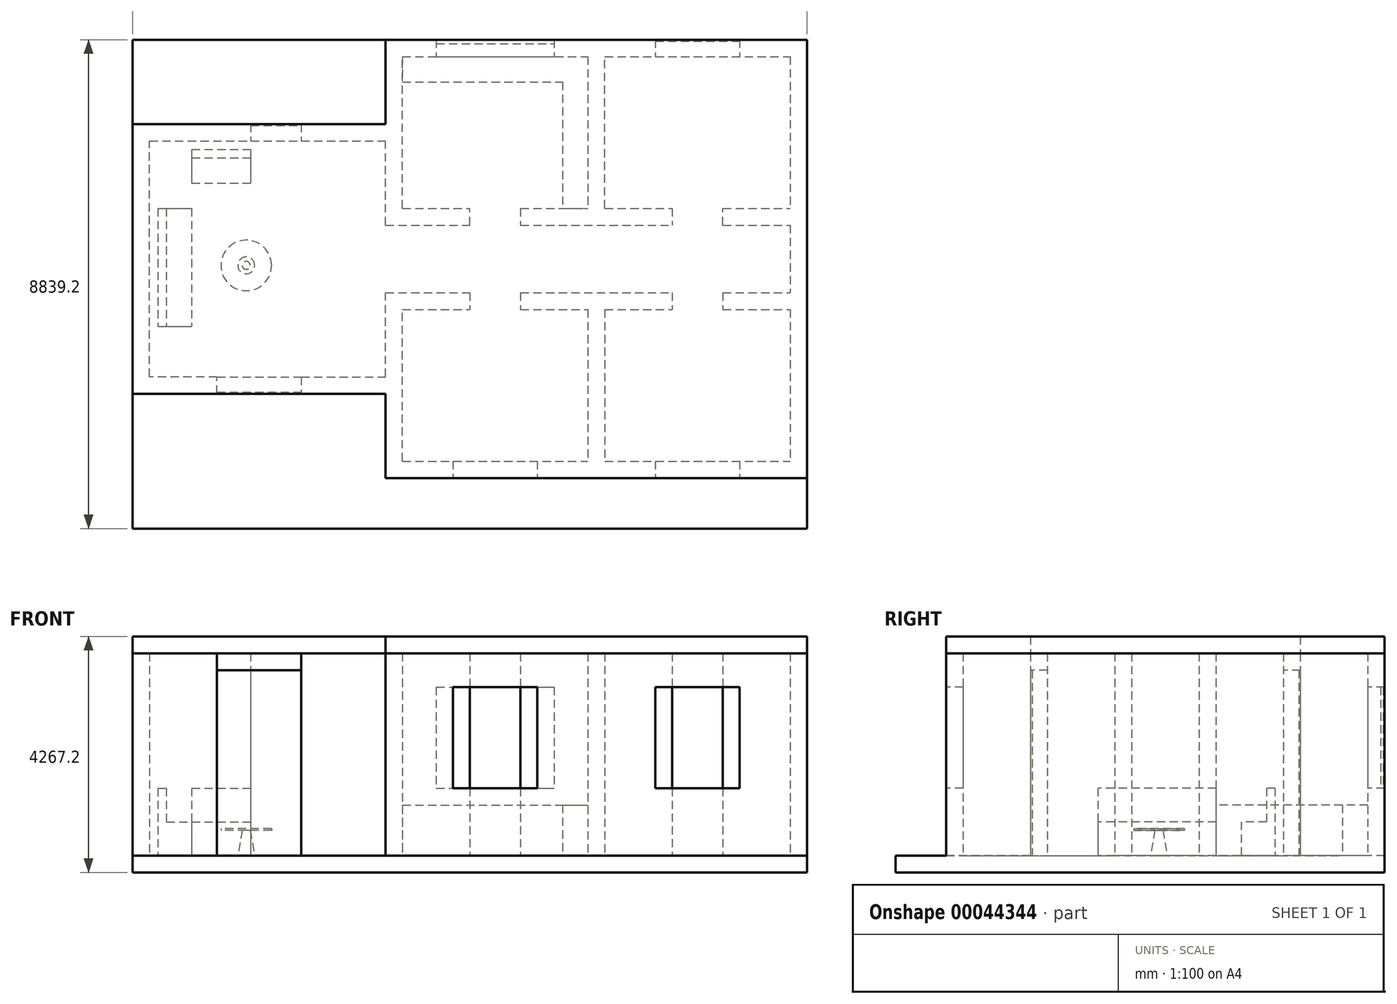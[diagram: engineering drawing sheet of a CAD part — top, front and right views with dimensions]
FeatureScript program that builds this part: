
annotation { "Feature Type Name" : "Feature", "Feature Type Description" : "" }
export const myFeature = defineFeature(function(context is Context, id is Id, definition is map)
    precondition{}
    {
        {
            var Q0;
            Q0=qCreatedBy(makeId("Top.planeOp"),FACE);
            var sketch = newSketch(context, id + "F0", { "sketchPlane" : qUnion([Q0])});
            skLineSegment(sketch, "E0", {"start": v(-1524, -1642.32) * mm, "end": v(0, -1642.32) * mm});
            skLineSegment(sketch, "E1", {"start": v(0, -1642.32) * mm, "end": v(0, -1337.52) * mm});
            skLineSegment(sketch, "E2", {"start": v(0, -1337.52) * mm, "end": v(-1524, -1337.52) * mm});
            skLineSegment(sketch, "E3", {"start": v(-1524, -1337.52) * mm, "end": v(-1524, -1642.32) * mm});
            skLineSegment(sketch, "E4.bottom", {"start": v(1524, -1337.52) * mm, "end": v(3048, -1337.52) * mm});
            skLineSegment(sketch, "E4.top", {"start": v(1524, -1642.32) * mm, "end": v(3048, -1642.32) * mm});
            skLineSegment(sketch, "E4.left", {"start": v(1524, -1337.52) * mm, "end": v(1524, -1642.32) * mm});
            skLineSegment(sketch, "E4.right", {"start": v(3048, -1337.52) * mm, "end": v(3048, -1642.32) * mm});
            skLineSegment(sketch, "E5.bottom", {"start": v(-1524, -1337.52) * mm, "end": v(-1219.2, -1337.52) * mm});
            skLineSegment(sketch, "E5.top", {"start": v(-1524, 3234.48) * mm, "end": v(-1219.2, 3234.48) * mm});
            skLineSegment(sketch, "E5.left", {"start": v(-1524, -1337.52) * mm, "end": v(-1524, 3234.48) * mm});
            skLineSegment(sketch, "E5.right", {"start": v(-1219.2, -1337.52) * mm, "end": v(-1219.2, 3234.48) * mm});
            skLineSegment(sketch, "E6.bottom", {"start": v(-1219.2, 3234.48) * mm, "end": v(609.6, 3234.48) * mm});
            skLineSegment(sketch, "E6.top", {"start": v(-1219.2, 2929.68) * mm, "end": v(609.6, 2929.68) * mm});
            skLineSegment(sketch, "E6.left", {"start": v(-1219.2, 3234.48) * mm, "end": v(-1219.2, 2929.68) * mm});
            skLineSegment(sketch, "E6.right", {"start": v(609.6, 3234.48) * mm, "end": v(609.6, 2929.68) * mm});
            skLineSegment(sketch, "E7.bottom", {"start": v(1524, 3234.48) * mm, "end": v(3048, 3234.48) * mm});
            skLineSegment(sketch, "E7.top", {"start": v(1524, 2929.68) * mm, "end": v(3048, 2929.68) * mm});
            skLineSegment(sketch, "E7.left", {"start": v(1524, 3234.48) * mm, "end": v(1524, 2929.68) * mm});
            skLineSegment(sketch, "E7.right", {"start": v(3048, 3234.48) * mm, "end": v(3048, 2929.68) * mm});
            skLineSegment(sketch, "E8.bottom", {"start": v(3048, -3166.32) * mm, "end": v(3352.8, -3166.32) * mm});
            skLineSegment(sketch, "E8.top", {"start": v(3048, 186.48) * mm, "end": v(3352.8, 186.48) * mm});
            skLineSegment(sketch, "E8.left", {"start": v(3048, -3166.32) * mm, "end": v(3048, 186.48) * mm});
            skLineSegment(sketch, "E8.right", {"start": v(3352.8, -3166.32) * mm, "end": v(3352.8, 186.48) * mm});
            skLineSegment(sketch, "E9.bottom", {"start": v(3352.8, 1405.68) * mm, "end": v(3048, 1405.68) * mm});
            skLineSegment(sketch, "E9.top", {"start": v(3352.8, 4758.48) * mm, "end": v(3048, 4758.48) * mm});
            skLineSegment(sketch, "E9.left", {"start": v(3352.8, 1405.68) * mm, "end": v(3352.8, 4758.48) * mm});
            skLineSegment(sketch, "E9.right", {"start": v(3048, 1405.68) * mm, "end": v(3048, 4758.48) * mm});
            skLineSegment(sketch, "E10.bottom", {"start": v(3352.8, 1405.68) * mm, "end": v(4572, 1405.68) * mm});
            skLineSegment(sketch, "E10.top", {"start": v(3352.8, 1710.48) * mm, "end": v(4572, 1710.48) * mm});
            skLineSegment(sketch, "E10.left", {"start": v(3352.8, 1405.68) * mm, "end": v(3352.8, 1710.48) * mm});
            skLineSegment(sketch, "E10.right", {"start": v(4572, 1405.68) * mm, "end": v(4572, 1710.48) * mm});
            skLineSegment(sketch, "E11.bottom", {"start": v(5486.4, 1710.48) * mm, "end": v(6705.6, 1710.48) * mm});
            skLineSegment(sketch, "E11.top", {"start": v(5486.4, 1405.68) * mm, "end": v(6705.6, 1405.68) * mm});
            skLineSegment(sketch, "E11.left", {"start": v(5486.4, 1710.48) * mm, "end": v(5486.4, 1405.68) * mm});
            skLineSegment(sketch, "E11.right", {"start": v(6705.6, 1710.48) * mm, "end": v(6705.6, 1405.68) * mm});
            skLineSegment(sketch, "E12.bottom", {"start": v(6705.6, 1405.68) * mm, "end": v(7010.4, 1405.68) * mm});
            skLineSegment(sketch, "E12.top", {"start": v(6705.6, 4758.48) * mm, "end": v(7010.4, 4758.48) * mm});
            skLineSegment(sketch, "E12.left", {"start": v(6705.6, 1405.68) * mm, "end": v(6705.6, 4758.48) * mm});
            skLineSegment(sketch, "E12.right", {"start": v(7010.4, 1405.68) * mm, "end": v(7010.4, 4758.48) * mm});
            skLineSegment(sketch, "E13.bottom", {"start": v(3352.8, 4758.48) * mm, "end": v(3962.4, 4758.48) * mm});
            skLineSegment(sketch, "E13.top", {"start": v(3352.8, 4453.68) * mm, "end": v(3962.4, 4453.68) * mm});
            skLineSegment(sketch, "E13.left", {"start": v(3352.8, 4758.48) * mm, "end": v(3352.8, 4453.68) * mm});
            skLineSegment(sketch, "E13.right", {"start": v(3962.4, 4758.48) * mm, "end": v(3962.4, 4453.68) * mm});
            skLineSegment(sketch, "E14.bottom", {"start": v(6096, 4758.48) * mm, "end": v(6705.6, 4758.48) * mm});
            skLineSegment(sketch, "E14.top", {"start": v(6096, 4453.68) * mm, "end": v(6705.6, 4453.68) * mm});
            skLineSegment(sketch, "E14.left", {"start": v(6096, 4758.48) * mm, "end": v(6096, 4453.68) * mm});
            skLineSegment(sketch, "E14.right", {"start": v(6705.6, 4758.48) * mm, "end": v(6705.6, 4453.68) * mm});
            skLineSegment(sketch, "E15.bottom", {"start": v(3352.8, 186.48) * mm, "end": v(4572, 186.48) * mm});
            skLineSegment(sketch, "E15.top", {"start": v(3352.8, -118.32) * mm, "end": v(4572, -118.32) * mm});
            skLineSegment(sketch, "E15.left", {"start": v(3352.8, 186.48) * mm, "end": v(3352.8, -118.32) * mm});
            skLineSegment(sketch, "E15.right", {"start": v(4572, 186.48) * mm, "end": v(4572, -118.32) * mm});
            skLineSegment(sketch, "E16.bottom", {"start": v(5486.4, 186.48) * mm, "end": v(6705.6, 186.48) * mm});
            skLineSegment(sketch, "E16.top", {"start": v(5486.4, -118.32) * mm, "end": v(6705.6, -118.32) * mm});
            skLineSegment(sketch, "E16.left", {"start": v(5486.4, 186.48) * mm, "end": v(5486.4, -118.32) * mm});
            skLineSegment(sketch, "E16.right", {"start": v(6705.6, 186.48) * mm, "end": v(6705.6, -118.32) * mm});
            skLineSegment(sketch, "E17.bottom", {"start": v(6705.6, 186.48) * mm, "end": v(7010.4, 186.48) * mm});
            skLineSegment(sketch, "E17.top", {"start": v(6705.6, -3166.32) * mm, "end": v(7010.4, -3166.32) * mm});
            skLineSegment(sketch, "E17.left", {"start": v(6705.6, 186.48) * mm, "end": v(6705.6, -3166.32) * mm});
            skLineSegment(sketch, "E17.right", {"start": v(7010.4, 186.48) * mm, "end": v(7010.4, -3166.32) * mm});
            skLineSegment(sketch, "E18.left", {"start": v(3352.8, -3166.32) * mm, "end": v(3352.8, -2861.52) * mm});
            skLineSegment(sketch, "E19.left", {"start": v(6705.6, -3166.32) * mm, "end": v(6705.6, -2861.52) * mm});
            skLineSegment(sketch, "E20.bottom", {"start": v(7010.4, 4758.48) * mm, "end": v(7924.8, 4758.48) * mm});
            skLineSegment(sketch, "E20.top", {"start": v(7010.4, 4453.68) * mm, "end": v(7924.8, 4453.68) * mm});
            skLineSegment(sketch, "E20.left", {"start": v(7010.4, 4758.48) * mm, "end": v(7010.4, 4453.68) * mm});
            skLineSegment(sketch, "E20.right", {"start": v(7924.8, 4758.48) * mm, "end": v(7924.8, 4453.68) * mm});
            skLineSegment(sketch, "E21.bottom", {"start": v(9448.8, 4758.48) * mm, "end": v(10363.2, 4758.48) * mm});
            skLineSegment(sketch, "E21.top", {"start": v(9448.8, 4453.68) * mm, "end": v(10363.2, 4453.68) * mm});
            skLineSegment(sketch, "E21.left", {"start": v(9448.8, 4758.48) * mm, "end": v(9448.8, 4453.68) * mm});
            skLineSegment(sketch, "E21.right", {"start": v(10363.2, 4758.48) * mm, "end": v(10363.2, 4453.68) * mm});
            skLineSegment(sketch, "E22.bottom", {"start": v(10363.2, 4758.48) * mm, "end": v(10668, 4758.48) * mm});
            skLineSegment(sketch, "E22.top", {"start": v(10363.2, 1405.68) * mm, "end": v(10668, 1405.68) * mm});
            skLineSegment(sketch, "E22.left", {"start": v(10363.2, 4758.48) * mm, "end": v(10363.2, 1405.68) * mm});
            skLineSegment(sketch, "E22.right", {"start": v(10668, 4758.48) * mm, "end": v(10668, 1405.68) * mm});
            skPoint(sketch, "E23.oppositeSnap0", {"position": v(6858, 1405.68) * mm});
            skLineSegment(sketch, "E23.bottom", {"start": v(7010.4, 1710.48) * mm, "end": v(8229.6, 1710.48) * mm});
            skLineSegment(sketch, "E23.top", {"start": v(7010.4, 1405.68) * mm, "end": v(8229.6, 1405.68) * mm});
            skLineSegment(sketch, "E23.left", {"start": v(7010.4, 1710.48) * mm, "end": v(7010.4, 1405.68) * mm});
            skLineSegment(sketch, "E23.right", {"start": v(8229.6, 1710.48) * mm, "end": v(8229.6, 1405.68) * mm});
            skLineSegment(sketch, "E24.bottom", {"start": v(9144, 1405.68) * mm, "end": v(10363.2, 1405.68) * mm});
            skLineSegment(sketch, "E24.top", {"start": v(9144, 1710.48) * mm, "end": v(10363.2, 1710.48) * mm});
            skLineSegment(sketch, "E24.left", {"start": v(9144, 1405.68) * mm, "end": v(9144, 1710.48) * mm});
            skLineSegment(sketch, "E24.right", {"start": v(10363.2, 1405.68) * mm, "end": v(10363.2, 1710.48) * mm});
            skLineSegment(sketch, "E25.bottom", {"start": v(7010.4, 186.48) * mm, "end": v(8229.6, 186.48) * mm});
            skLineSegment(sketch, "E25.top", {"start": v(7010.4, -118.32) * mm, "end": v(8229.6, -118.32) * mm});
            skLineSegment(sketch, "E25.left", {"start": v(7010.4, 186.48) * mm, "end": v(7010.4, -118.32) * mm});
            skLineSegment(sketch, "E25.right", {"start": v(8229.6, 186.48) * mm, "end": v(8229.6, -118.32) * mm});
            skLineSegment(sketch, "E26.bottom", {"start": v(9144, 186.48) * mm, "end": v(10363.2, 186.48) * mm});
            skLineSegment(sketch, "E26.top", {"start": v(9144, -118.32) * mm, "end": v(10363.2, -118.32) * mm});
            skLineSegment(sketch, "E26.left", {"start": v(9144, 186.48) * mm, "end": v(9144, -118.32) * mm});
            skLineSegment(sketch, "E26.right", {"start": v(10363.2, 186.48) * mm, "end": v(10363.2, -118.32) * mm});
            skLineSegment(sketch, "E27.bottom", {"start": v(7010.4, -3166.32) * mm, "end": v(7924.8, -3166.32) * mm});
            skLineSegment(sketch, "E27.top", {"start": v(7010.4, -2861.52) * mm, "end": v(7924.8, -2861.52) * mm});
            skLineSegment(sketch, "E27.left", {"start": v(7010.4, -3166.32) * mm, "end": v(7010.4, -2861.52) * mm});
            skLineSegment(sketch, "E27.right", {"start": v(7924.8, -3166.32) * mm, "end": v(7924.8, -2861.52) * mm});
            skLineSegment(sketch, "E28.bottom", {"start": v(9448.8, -2861.52) * mm, "end": v(10363.2, -2861.52) * mm});
            skLineSegment(sketch, "E28.top", {"start": v(9448.8, -3166.32) * mm, "end": v(10363.2, -3166.32) * mm});
            skLineSegment(sketch, "E28.left", {"start": v(9448.8, -2861.52) * mm, "end": v(9448.8, -3166.32) * mm});
            skLineSegment(sketch, "E28.right", {"start": v(10363.2, -2861.52) * mm, "end": v(10363.2, -3166.32) * mm});
            skLineSegment(sketch, "E29.top", {"start": v(10363.2, -3166.32) * mm, "end": v(10668, -3166.32) * mm});
            skLineSegment(sketch, "E29.left", {"start": v(10363.2, 1405.68) * mm, "end": v(10363.2, -3166.32) * mm});
            skLineSegment(sketch, "E29.right", {"start": v(10668, 1405.68) * mm, "end": v(10668, -3166.32) * mm});
            skLineSegment(sketch, "E30.bottom", {"start": v(3352.8, -2861.52) * mm, "end": v(4267.2, -2861.52) * mm});
            skLineSegment(sketch, "E30.top", {"start": v(3352.8, -3166.32) * mm, "end": v(4267.2, -3166.32) * mm});
            skLineSegment(sketch, "E30.left", {"start": v(3352.8, -2861.52) * mm, "end": v(3352.8, -3166.32) * mm});
            skLineSegment(sketch, "E30.right", {"start": v(4267.2, -2861.52) * mm, "end": v(4267.2, -3166.32) * mm});
            skLineSegment(sketch, "E31.bottom", {"start": v(6705.6, -2861.52) * mm, "end": v(5791.2, -2861.52) * mm});
            skLineSegment(sketch, "E31.top", {"start": v(6705.6, -3166.32) * mm, "end": v(5791.2, -3166.32) * mm});
            skLineSegment(sketch, "E31.left", {"start": v(6705.6, -2861.52) * mm, "end": v(6705.6, -3166.32) * mm});
            skLineSegment(sketch, "E31.right", {"start": v(5791.2, -2861.52) * mm, "end": v(5791.2, -3166.32) * mm});
            skSolve(sketch);
        }
        {
            var Q0;
            Q0 = qSketchRegion(id + "F0", true);
            extrude(context, id + "F1", {"entities" : qUnion([Q0]), "depth" : 3657.6 * mm});
        }
        {
            var Q0;
            Q0=qCreatedBy(makeId("Top.planeOp"),FACE);
            var sketch = newSketch(context, id + "F2", { "sketchPlane" : qUnion([Q0])});
            skLineSegment(sketch, "E32.bottom", {"start": v(-1524, 4758.48) * mm, "end": v(10668, 4758.48) * mm});
            skLineSegment(sketch, "E32.top", {"start": v(-1524, -3166.32) * mm, "end": v(10668, -3166.32) * mm});
            skLineSegment(sketch, "E32.left", {"start": v(-1524, 4758.48) * mm, "end": v(-1524, -3166.32) * mm});
            skLineSegment(sketch, "E32.right", {"start": v(10668, 4758.48) * mm, "end": v(10668, -3166.32) * mm});
            skLineSegment(sketch, "E33.top", {"start": v(-1524, -4080.72) * mm, "end": v(10668, -4080.72) * mm});
            skLineSegment(sketch, "E33.left", {"start": v(-1524, -3166.32) * mm, "end": v(-1524, -4080.72) * mm});
            skLineSegment(sketch, "E33.right", {"start": v(10668, -3166.32) * mm, "end": v(10668, -4080.72) * mm});
            skSolve(sketch);
        }
        {
            var Q0;
            Q0 = qSketchRegion(id + "F2", true);
            extrude(context, id + "F3", {"entities" : qUnion([Q0]), "oppositeDirection" : true, "depth" : 304.8 * mm});
        }
        {
            var Q0;
            Q0=qCreatedBy(makeId("Top.planeOp"),FACE);
            var sketch = newSketch(context, id + "F4", { "sketchPlane" : qUnion([Q0])});
            skLineSegment(sketch, "E34.bottom", {"start": v(3962.4, 4758.48) * mm, "end": v(6096, 4758.48) * mm});
            skLineSegment(sketch, "E34.top", {"start": v(3962.4, 4453.68) * mm, "end": v(6096, 4453.68) * mm});
            skLineSegment(sketch, "E34.left", {"start": v(3962.4, 4758.48) * mm, "end": v(3962.4, 4453.68) * mm});
            skLineSegment(sketch, "E34.right", {"start": v(6096, 4758.48) * mm, "end": v(6096, 4453.68) * mm});
            skLineSegment(sketch, "E35.bottom", {"start": v(7924.8, -2861.52) * mm, "end": v(9448.8, -2861.52) * mm});
            skLineSegment(sketch, "E35.top", {"start": v(7924.8, -3166.32) * mm, "end": v(9448.8, -3166.32) * mm});
            skLineSegment(sketch, "E35.left", {"start": v(7924.8, -2861.52) * mm, "end": v(7924.8, -3166.32) * mm});
            skLineSegment(sketch, "E35.right", {"start": v(9448.8, -2861.52) * mm, "end": v(9448.8, -3166.32) * mm});
            skLineSegment(sketch, "E36.bottom", {"start": v(4267.2, -2861.52) * mm, "end": v(5791.2, -2861.52) * mm});
            skLineSegment(sketch, "E36.top", {"start": v(4267.2, -3166.32) * mm, "end": v(5791.2, -3166.32) * mm});
            skLineSegment(sketch, "E36.left", {"start": v(4267.2, -2861.52) * mm, "end": v(4267.2, -3166.32) * mm});
            skLineSegment(sketch, "E36.right", {"start": v(5791.2, -2861.52) * mm, "end": v(5791.2, -3166.32) * mm});
            skSolve(sketch);
        }
        {
            var Q0;
            Q0 = qSketchRegion(id + "F4", true);
            extrude(context, id + "F5", {"entities" : qUnion([Q0]), "depth" : 1219.2 * mm});
        }
        {
            var Q0;
            Q0=qCreatedBy(makeId("Top.planeOp"),FACE);
            cPlane(context, id + "F6", {"entities" : qUnion([Q0]), "cplaneType" : CPlaneType.OFFSET, "offset" : 3048 * mm, "width" : 152.4 * mm, "height" : 152.4 * mm});
        }
        {
            var Q0;
            Q0=qCreatedBy(id+"F6.planeOp",FACE);
            var sketch = newSketch(context, id + "F7", { "sketchPlane" : qUnion([Q0])});
            skLineSegment(sketch, "E37.bottom", {"start": v(3962.4, 4758.48) * mm, "end": v(6096, 4758.48) * mm});
            skLineSegment(sketch, "E37.top", {"start": v(3962.4, 4453.68) * mm, "end": v(6096, 4453.68) * mm});
            skLineSegment(sketch, "E37.left", {"start": v(3962.4, 4758.48) * mm, "end": v(3962.4, 4453.68) * mm});
            skLineSegment(sketch, "E37.right", {"start": v(6096, 4758.48) * mm, "end": v(6096, 4453.68) * mm});
            skLineSegment(sketch, "E38.bottom", {"start": v(7924.8, 4758.48) * mm, "end": v(9448.8, 4758.48) * mm});
            skLineSegment(sketch, "E38.top", {"start": v(7924.8, 4453.68) * mm, "end": v(9448.8, 4453.68) * mm});
            skLineSegment(sketch, "E38.left", {"start": v(7924.8, 4758.48) * mm, "end": v(7924.8, 4453.68) * mm});
            skLineSegment(sketch, "E38.right", {"start": v(9448.8, 4758.48) * mm, "end": v(9448.8, 4453.68) * mm});
            skLineSegment(sketch, "E39.bottom", {"start": v(7924.8, -2861.52) * mm, "end": v(9448.8, -2861.52) * mm});
            skLineSegment(sketch, "E39.top", {"start": v(7924.8, -3166.32) * mm, "end": v(9448.8, -3166.32) * mm});
            skLineSegment(sketch, "E39.left", {"start": v(7924.8, -2861.52) * mm, "end": v(7924.8, -3166.32) * mm});
            skLineSegment(sketch, "E39.right", {"start": v(9448.8, -2861.52) * mm, "end": v(9448.8, -3166.32) * mm});
            skLineSegment(sketch, "E40.bottom", {"start": v(4267.2, -2861.52) * mm, "end": v(5791.2, -2861.52) * mm});
            skLineSegment(sketch, "E40.top", {"start": v(4267.2, -3166.32) * mm, "end": v(5791.2, -3166.32) * mm});
            skLineSegment(sketch, "E40.left", {"start": v(4267.2, -2861.52) * mm, "end": v(4267.2, -3166.32) * mm});
            skLineSegment(sketch, "E40.right", {"start": v(5791.2, -2861.52) * mm, "end": v(5791.2, -3166.32) * mm});
            skSolve(sketch);
        }
        {
            var Q0;
            Q0 = qSketchRegion(id + "F7", true);
            var Q1;
            Q1=makeQuery(id+"F1.opExtrude","CAP_FACE",FACE,{"disambiguationData":[OSD([sQuery(id+"F0.wireOp",EDGE,"E4.bottom"),sQuery(id+"F0.wireOp",EDGE,"E4.top"),sQuery(id+"F0.wireOp",EDGE,"E4.left"),sQuery(id+"F0.wireOp",EDGE,"E8.bottom"),sQuery(id+"F0.wireOp",EDGE,"E8.top"),sQuery(id+"F0.wireOp",EDGE,"E8.left"),sQuery(id+"F0.wireOp",EDGE,"E8.right"),sQuery(id+"F0.wireOp",EDGE,"E15.bottom"),sQuery(id+"F0.wireOp",EDGE,"E15.top"),sQuery(id+"F0.wireOp",EDGE,"E15.right"),sQuery(id+"F0.wireOp",EDGE,"E18.bottom"),sQuery(id+"F0.wireOp",EDGE,"E18.top"),sQuery(id+"F0.wireOp",EDGE,"E18.right")])],"isStart":false});
            extrude(context, id + "F8", {"entities" : qUnion([Q0]), "depth" : 609.6 * mm});
        }
        {
            var Q0;
            Q0=qCreatedBy(makeId("Top.planeOp"),FACE);
            cPlane(context, id + "F9", {"entities" : qUnion([Q0]), "cplaneType" : CPlaneType.OFFSET, "offset" : 3657.6 * mm, "width" : 152.4 * mm, "height" : 152.4 * mm});
        }
        {
            var Q0;
            Q0=qCreatedBy(id+"F9.planeOp",FACE);
            var sketch = newSketch(context, id + "F10", { "sketchPlane" : qUnion([Q0])});
            skLineSegment(sketch, "E41", {"start": v(-1524, 3234.48) * mm, "end": v(-1524, -1642.32) * mm});
            skLineSegment(sketch, "E42", {"start": v(-1524, -1642.32) * mm, "end": v(3048, -1642.32) * mm});
            skLineSegment(sketch, "E43", {"start": v(3048, -1642.32) * mm, "end": v(3048, -3166.32) * mm});
            skLineSegment(sketch, "E44", {"start": v(3048, -3166.32) * mm, "end": v(10668, -3166.32) * mm});
            skLineSegment(sketch, "E45", {"start": v(10668, -3166.32) * mm, "end": v(10668, 4758.48) * mm});
            skLineSegment(sketch, "E46", {"start": v(10668, 4758.48) * mm, "end": v(3048, 4758.48) * mm});
            skLineSegment(sketch, "E47", {"start": v(3048, 4758.48) * mm, "end": v(3048, 3234.48) * mm});
            skLineSegment(sketch, "E48", {"start": v(3048, 3234.48) * mm, "end": v(-1524, 3234.48) * mm});
            skSolve(sketch);
        }
        {
            var Q0;
            Q0 = qSketchRegion(id + "F10", true);
            extrude(context, id + "F11", {"entities" : qUnion([Q0]), "depth" : 304.8 * mm});
        }
        {
            var Q0;
            Q0=makeQuery(id+"F1.opExtrude","SWEPT_BODY",BODY,{"disambiguationData":[OSD([sQuery(id+"F0.wireOp",EDGE,"E0"),sQuery(id+"F0.wireOp",EDGE,"E1"),sQuery(id+"F0.wireOp",EDGE,"E2"),sQuery(id+"F0.wireOp",EDGE,"E3"),sQuery(id+"F0.wireOp",EDGE,"E5.top"),sQuery(id+"F0.wireOp",EDGE,"E5.left"),sQuery(id+"F0.wireOp",EDGE,"E5.right"),sQuery(id+"F0.wireOp",EDGE,"E6.bottom"),sQuery(id+"F0.wireOp",EDGE,"E6.top"),sQuery(id+"F0.wireOp",EDGE,"E6.right")])]});
            var Q1;
            Q1=makeQuery(id+"F1.opExtrude","SWEPT_BODY",BODY,{"disambiguationData":[OSD([sQuery(id+"F0.wireOp",EDGE,"E4.bottom"),sQuery(id+"F0.wireOp",EDGE,"E4.top"),sQuery(id+"F0.wireOp",EDGE,"E4.left"),sQuery(id+"F0.wireOp",EDGE,"E8.bottom"),sQuery(id+"F0.wireOp",EDGE,"E8.top"),sQuery(id+"F0.wireOp",EDGE,"E8.left"),sQuery(id+"F0.wireOp",EDGE,"E8.right"),sQuery(id+"F0.wireOp",EDGE,"E15.bottom"),sQuery(id+"F0.wireOp",EDGE,"E15.top"),sQuery(id+"F0.wireOp",EDGE,"E15.right"),sQuery(id+"F0.wireOp",EDGE,"E18.bottom"),sQuery(id+"F0.wireOp",EDGE,"E18.top"),sQuery(id+"F0.wireOp",EDGE,"E18.right")])]});
            var Q2;
            Q2=makeQuery(id+"F1.opExtrude","SWEPT_BODY",BODY,{"disambiguationData":[OSD([sQuery(id+"F0.wireOp",EDGE,"E7.bottom"),sQuery(id+"F0.wireOp",EDGE,"E7.top"),sQuery(id+"F0.wireOp",EDGE,"E7.left"),sQuery(id+"F0.wireOp",EDGE,"E9.bottom"),sQuery(id+"F0.wireOp",EDGE,"E9.top"),sQuery(id+"F0.wireOp",EDGE,"E9.left"),sQuery(id+"F0.wireOp",EDGE,"E9.right"),sQuery(id+"F0.wireOp",EDGE,"E10.bottom"),sQuery(id+"F0.wireOp",EDGE,"E10.top"),sQuery(id+"F0.wireOp",EDGE,"E10.right"),sQuery(id+"F0.wireOp",EDGE,"E13.bottom"),sQuery(id+"F0.wireOp",EDGE,"E13.top"),sQuery(id+"F0.wireOp",EDGE,"E13.right")])]});
            var Q3;
            Q3=makeQuery(id+"F1.opExtrude","SWEPT_BODY",BODY,{"disambiguationData":[OSD([sQuery(id+"F0.wireOp",EDGE,"E11.bottom"),sQuery(id+"F0.wireOp",EDGE,"E11.top"),sQuery(id+"F0.wireOp",EDGE,"E11.left"),sQuery(id+"F0.wireOp",EDGE,"E12.bottom"),sQuery(id+"F0.wireOp",EDGE,"E12.top"),sQuery(id+"F0.wireOp",EDGE,"E12.left"),sQuery(id+"F0.wireOp",EDGE,"E12.right"),sQuery(id+"F0.wireOp",EDGE,"E14.bottom"),sQuery(id+"F0.wireOp",EDGE,"E14.top"),sQuery(id+"F0.wireOp",EDGE,"E14.left"),sQuery(id+"F0.wireOp",EDGE,"E20.bottom"),sQuery(id+"F0.wireOp",EDGE,"E20.top"),sQuery(id+"F0.wireOp",EDGE,"E20.right"),sQuery(id+"F0.wireOp",EDGE,"E23.bottom"),sQuery(id+"F0.wireOp",EDGE,"E23.top"),sQuery(id+"F0.wireOp",EDGE,"E23.right")])]});
            var Q4;
            Q4=makeQuery(id+"F1.opExtrude","SWEPT_BODY",BODY,{"disambiguationData":[OSD([sQuery(id+"F0.wireOp",EDGE,"E16.bottom"),sQuery(id+"F0.wireOp",EDGE,"E16.top"),sQuery(id+"F0.wireOp",EDGE,"E16.left"),sQuery(id+"F0.wireOp",EDGE,"E17.bottom"),sQuery(id+"F0.wireOp",EDGE,"E17.top"),sQuery(id+"F0.wireOp",EDGE,"E17.left"),sQuery(id+"F0.wireOp",EDGE,"E17.right"),sQuery(id+"F0.wireOp",EDGE,"E19.bottom"),sQuery(id+"F0.wireOp",EDGE,"E19.top"),sQuery(id+"F0.wireOp",EDGE,"E19.right"),sQuery(id+"F0.wireOp",EDGE,"E25.bottom"),sQuery(id+"F0.wireOp",EDGE,"E25.top"),sQuery(id+"F0.wireOp",EDGE,"E25.right"),sQuery(id+"F0.wireOp",EDGE,"E27.bottom"),sQuery(id+"F0.wireOp",EDGE,"E27.top"),sQuery(id+"F0.wireOp",EDGE,"E27.right")])]});
            var Q5;
            Q5=makeQuery(id+"F1.opExtrude","SWEPT_BODY",BODY,{"disambiguationData":[OSD([sQuery(id+"F0.wireOp",EDGE,"E21.bottom"),sQuery(id+"F0.wireOp",EDGE,"E21.top"),sQuery(id+"F0.wireOp",EDGE,"E21.left"),sQuery(id+"F0.wireOp",EDGE,"E22.bottom"),sQuery(id+"F0.wireOp",EDGE,"E22.top"),sQuery(id+"F0.wireOp",EDGE,"E22.left"),sQuery(id+"F0.wireOp",EDGE,"E22.right"),sQuery(id+"F0.wireOp",EDGE,"E24.bottom"),sQuery(id+"F0.wireOp",EDGE,"E24.top"),sQuery(id+"F0.wireOp",EDGE,"E24.left")])]});
            var Q6;
            Q6=makeQuery(id+"F1.opExtrude","SWEPT_BODY",BODY,{"disambiguationData":[OSD([sQuery(id+"F0.wireOp",EDGE,"E26.bottom"),sQuery(id+"F0.wireOp",EDGE,"E26.top"),sQuery(id+"F0.wireOp",EDGE,"E26.left"),sQuery(id+"F0.wireOp",EDGE,"E26.right")])]});
            var Q7;
            Q7=makeQuery(id+"F1.opExtrude","SWEPT_BODY",BODY,{"disambiguationData":[OSD([sQuery(id+"F0.wireOp",EDGE,"E28.bottom"),sQuery(id+"F0.wireOp",EDGE,"E28.top"),sQuery(id+"F0.wireOp",EDGE,"E28.left"),sQuery(id+"F0.wireOp",EDGE,"E28.right")])]});
            var Q8;
            Q8=makeQuery(id+"F1.opExtrude","SWEPT_BODY",BODY,{"disambiguationData":[OSD([sQuery(id+"F0.wireOp",EDGE,"E22.top"),sQuery(id+"F0.wireOp",EDGE,"E29.top"),sQuery(id+"F0.wireOp",EDGE,"E29.left"),sQuery(id+"F0.wireOp",EDGE,"E29.right")])]});
            var Q9;
            Q9=makeQuery(id+"F3.opExtrude","SWEPT_BODY",BODY,{"disambiguationData":[OSD([sQuery(id+"F2.wireOp",EDGE,"E32.bottom"),sQuery(id+"F2.wireOp",EDGE,"E32.top"),sQuery(id+"F2.wireOp",EDGE,"E32.left"),sQuery(id+"F2.wireOp",EDGE,"E32.right")])]});
            var Q10;
            Q10=makeQuery(id+"F5.opExtrude","SWEPT_BODY",BODY,{"disambiguationData":[OSD([sQuery(id+"F4.wireOp",EDGE,"E34.bottom"),sQuery(id+"F4.wireOp",EDGE,"E34.top"),sQuery(id+"F4.wireOp",EDGE,"E34.left"),sQuery(id+"F4.wireOp",EDGE,"E34.right")])]});
            var Q11;
            Q11=makeQuery(id+"F5.opExtrude","SWEPT_BODY",BODY,{"disambiguationData":[OSD([sQuery(id+"F4.wireOp",EDGE,"46e9026d-46fc-4155-8c71-2280dcd3004d.bottom"),sQuery(id+"F4.wireOp",EDGE,"46e9026d-46fc-4155-8c71-2280dcd3004d.top"),sQuery(id+"F4.wireOp",EDGE,"46e9026d-46fc-4155-8c71-2280dcd3004d.left"),sQuery(id+"F4.wireOp",EDGE,"46e9026d-46fc-4155-8c71-2280dcd3004d.right")])]});
            var Q12;
            Q12=makeQuery(id+"F5.opExtrude","SWEPT_BODY",BODY,{"disambiguationData":[OSD([sQuery(id+"F4.wireOp",EDGE,"E35.bottom"),sQuery(id+"F4.wireOp",EDGE,"E35.top"),sQuery(id+"F4.wireOp",EDGE,"E35.left"),sQuery(id+"F4.wireOp",EDGE,"E35.right")])]});
            var Q13;
            Q13=makeQuery(id+"F5.opExtrude","SWEPT_BODY",BODY,{"disambiguationData":[OSD([sQuery(id+"F4.wireOp",EDGE,"E36.bottom"),sQuery(id+"F4.wireOp",EDGE,"E36.top"),sQuery(id+"F4.wireOp",EDGE,"E36.left"),sQuery(id+"F4.wireOp",EDGE,"E36.right")])]});
            var Q14;
            Q14=makeQuery(id+"F8.opExtrude","SWEPT_BODY",BODY,{"disambiguationData":[OSD([sQuery(id+"F7.wireOp",EDGE,"E37.bottom"),sQuery(id+"F7.wireOp",EDGE,"E37.top"),sQuery(id+"F7.wireOp",EDGE,"E37.left"),sQuery(id+"F7.wireOp",EDGE,"E37.right")])]});
            var Q15;
            Q15=makeQuery(id+"F8.opExtrude","SWEPT_BODY",BODY,{"disambiguationData":[OSD([sQuery(id+"F7.wireOp",EDGE,"E38.bottom"),sQuery(id+"F7.wireOp",EDGE,"E38.top"),sQuery(id+"F7.wireOp",EDGE,"E38.left"),sQuery(id+"F7.wireOp",EDGE,"E38.right")])]});
            var Q16;
            Q16=makeQuery(id+"F8.opExtrude","SWEPT_BODY",BODY,{"disambiguationData":[OSD([sQuery(id+"F7.wireOp",EDGE,"E39.bottom"),sQuery(id+"F7.wireOp",EDGE,"E39.top"),sQuery(id+"F7.wireOp",EDGE,"E39.left"),sQuery(id+"F7.wireOp",EDGE,"E39.right")])]});
            var Q17;
            Q17=makeQuery(id+"F8.opExtrude","SWEPT_BODY",BODY,{"disambiguationData":[OSD([sQuery(id+"F7.wireOp",EDGE,"E40.bottom"),sQuery(id+"F7.wireOp",EDGE,"E40.top"),sQuery(id+"F7.wireOp",EDGE,"E40.left"),sQuery(id+"F7.wireOp",EDGE,"E40.right")])]});
            booleanBodies(context, id + "F12", {"operationType" : BooleanOperationType.UNION, "tools" : qUnion([Q0, Q1, Q2, Q3, Q4, Q5, Q6, Q7, Q8, Q9, Q10, Q11, Q12, Q13, Q14, Q15, Q16, Q17])});
        }
        {
            var Q0;
            Q0=qCreatedBy(makeId("Top.planeOp"),FACE);
            var sketch = newSketch(context, id + "F13", { "sketchPlane" : qUnion([Q0])});
            skLineSegment(sketch, "E49.bottom", {"start": v(0, -1642.32) * mm, "end": v(1524, -1642.32) * mm});
            skLineSegment(sketch, "E49.top", {"start": v(0, -1611.84) * mm, "end": v(1524, -1611.84) * mm});
            skLineSegment(sketch, "E49.left", {"start": v(0, -1642.32) * mm, "end": v(0, -1611.84) * mm});
            skLineSegment(sketch, "E49.right", {"start": v(1524, -1642.32) * mm, "end": v(1524, -1611.84) * mm});
            skLineSegment(sketch, "E50.bottom", {"start": v(609.6, 3234.48) * mm, "end": v(1524, 3234.48) * mm});
            skLineSegment(sketch, "E50.top", {"start": v(609.6, 3204) * mm, "end": v(1524, 3204) * mm});
            skLineSegment(sketch, "E50.left", {"start": v(609.6, 3234.48) * mm, "end": v(609.6, 3204) * mm});
            skLineSegment(sketch, "E50.right", {"start": v(1524, 3234.48) * mm, "end": v(1524, 3204) * mm});
            skSolve(sketch);
        }
        {
            var Q0;
            Q0 = qSketchRegion(id + "F13", true);
            extrude(context, id + "F14", {"entities" : qUnion([Q0]), "depth" : 3352.8 * mm});
        }
        {
            var Q0;
            Q0=qCreatedBy(makeId("Top.planeOp"),FACE);
            var sketch = newSketch(context, id + "F15", { "sketchPlane" : qUnion([Q0])});
            skLineSegment(sketch, "E51.bottom", {"start": v(7924.8, 4758.48) * mm, "end": v(9448.8, 4758.48) * mm});
            skLineSegment(sketch, "E51.top", {"start": v(7924.8, 4453.68) * mm, "end": v(9448.8, 4453.68) * mm});
            skLineSegment(sketch, "E51.left", {"start": v(7924.8, 4758.48) * mm, "end": v(7924.8, 4453.68) * mm});
            skLineSegment(sketch, "E51.right", {"start": v(9448.8, 4758.48) * mm, "end": v(9448.8, 4453.68) * mm});
            skSolve(sketch);
        }
        {
            var Q0;
            Q0 = qSketchRegion(id + "F15", true);
            extrude(context, id + "F16", {"entities" : qUnion([Q0]), "operationType" : NewBodyOperationType.ADD, "depth" : 1219.2 * mm});
        }
        {
            var Q0;
            Q0=qCreatedBy(makeId("Top.planeOp"),FACE);
            var sketch = newSketch(context, id + "F17", { "sketchPlane" : qUnion([Q0])});
            skLineSegment(sketch, "E52.bottom", {"start": v(3352.8, 4453.68) * mm, "end": v(6705.6, 4453.68) * mm});
            skLineSegment(sketch, "E52.top", {"start": v(3352.8, 3996.48) * mm, "end": v(6705.6, 3996.48) * mm});
            skLineSegment(sketch, "E52.left", {"start": v(3352.8, 4453.68) * mm, "end": v(3352.8, 3996.48) * mm});
            skLineSegment(sketch, "E52.right", {"start": v(6705.6, 4453.68) * mm, "end": v(6705.6, 3996.48) * mm});
            skLineSegment(sketch, "E53.bottom", {"start": v(6248.4, 3996.48) * mm, "end": v(6705.6, 3996.48) * mm});
            skLineSegment(sketch, "E53.top", {"start": v(6248.4, 1710.48) * mm, "end": v(6705.6, 1710.48) * mm});
            skLineSegment(sketch, "E53.left", {"start": v(6248.4, 3996.48) * mm, "end": v(6248.4, 1710.48) * mm});
            skLineSegment(sketch, "E53.right", {"start": v(6705.6, 3996.48) * mm, "end": v(6705.6, 1710.48) * mm});
            skSolve(sketch);
        }
        {
            var Q0;
            Q0 = qSketchRegion(id + "F17", true);
            extrude(context, id + "F18", {"entities" : qUnion([Q0]), "operationType" : NewBodyOperationType.ADD, "depth" : 914.4 * mm});
        }
        {
            var Q0;
            Q0=qCreatedBy(makeId("Top.planeOp"),FACE);
            var sketch = newSketch(context, id + "F19", { "sketchPlane" : qUnion([Q0])});
            skLineSegment(sketch, "E54.bottom", {"start": v(-457.2, 2777.28) * mm, "end": v(609.6, 2777.28) * mm});
            skLineSegment(sketch, "E54.top", {"start": v(-457.2, 2167.68) * mm, "end": v(609.6, 2167.68) * mm});
            skLineSegment(sketch, "E54.left", {"start": v(-457.2, 2777.28) * mm, "end": v(-457.2, 2167.68) * mm});
            skLineSegment(sketch, "E54.right", {"start": v(609.6, 2777.28) * mm, "end": v(609.6, 2167.68) * mm});
            skLineSegment(sketch, "E55.bottom", {"start": v(-1066.8, 1710.48) * mm, "end": v(-457.2, 1710.48) * mm});
            skLineSegment(sketch, "E55.top", {"start": v(-1066.8, -423.12) * mm, "end": v(-457.2, -423.12) * mm});
            skLineSegment(sketch, "E55.left", {"start": v(-1066.8, 1710.48) * mm, "end": v(-1066.8, -423.12) * mm});
            skLineSegment(sketch, "E55.right", {"start": v(-457.2, 1710.48) * mm, "end": v(-457.2, -423.12) * mm});
            skSolve(sketch);
        }
        {
            var Q0;
            Q0 = qSketchRegion(id + "F19", true);
            extrude(context, id + "F20", {"entities" : qUnion([Q0]), "operationType" : NewBodyOperationType.ADD, "depth" : 609.6 * mm});
        }
        {
            var Q0;
            Q0=makeQuery(id+"F20.opExtrude","CAP_FACE",FACE,{"disambiguationData":[OSD([sQuery(id+"F19.wireOp",EDGE,"E54.bottom"),sQuery(id+"F19.wireOp",EDGE,"E54.top"),sQuery(id+"F19.wireOp",EDGE,"E54.left"),sQuery(id+"F19.wireOp",EDGE,"E54.right")])],"isStart":false});
            var sketch = newSketch(context, id + "F21", { "sketchPlane" : qUnion([Q0])});
            skLineSegment(sketch, "E56.bottom", {"start": v(-457.2, 2777.28) * mm, "end": v(609.6, 2777.28) * mm});
            skLineSegment(sketch, "E56.top", {"start": v(-457.2, 2624.88) * mm, "end": v(609.6, 2624.88) * mm});
            skLineSegment(sketch, "E56.left", {"start": v(-457.2, 2777.28) * mm, "end": v(-457.2, 2624.88) * mm});
            skLineSegment(sketch, "E56.right", {"start": v(609.6, 2777.28) * mm, "end": v(609.6, 2624.88) * mm});
            skLineSegment(sketch, "E57.bottom", {"start": v(-1066.8, 1710.48) * mm, "end": v(-914.4, 1710.48) * mm});
            skLineSegment(sketch, "E57.top", {"start": v(-1066.8, -423.12) * mm, "end": v(-914.4, -423.12) * mm});
            skLineSegment(sketch, "E57.left", {"start": v(-1066.8, 1710.48) * mm, "end": v(-1066.8, -423.12) * mm});
            skLineSegment(sketch, "E57.right", {"start": v(-914.4, 1710.48) * mm, "end": v(-914.4, -423.12) * mm});
            skSolve(sketch);
        }
        {
            var Q0;
            Q0 = qSketchRegion(id + "F21", true);
            extrude(context, id + "F22", {"entities" : qUnion([Q0]), "operationType" : NewBodyOperationType.ADD, "depth" : 609.6 * mm});
        }
        {
            var Q0;
            Q0=qCreatedBy(makeId("Top.planeOp"),FACE);
            var sketch = newSketch(context, id + "F23", { "sketchPlane" : qUnion([Q0])});
            skCircle(sketch, "E58", {"center": v(527.59, 676.93) * mm, "radius": 152.4 * mm});
            skSolve(sketch);
        }
        {
            var Q0;
            Q0 = qSketchRegion(id + "F23", true);
            extrude(context, id + "F24", {"entities" : qUnion([Q0]), "operationType" : NewBodyOperationType.ADD, "depth" : 457.2 * mm, "hasDraft" : true, "draftAngle" : 10 * degree, "draftPullDirection" : true});
        }
        {
            var Q0;
            Q0=makeQuery(id+"F24.opExtrude","CAP_FACE",FACE,{"disambiguationData":[OSD([sQuery(id+"F23.wireOp",EDGE,"E58")])],"isStart":false});
            var sketch = newSketch(context, id + "F25", { "sketchPlane" : qUnion([Q0])});
            skCircle(sketch, "E59", {"center": v(527.59, 676.93) * mm, "radius": 457.2 * mm});
            skSolve(sketch);
        }
        {
            var Q0;
            Q0 = qSketchRegion(id + "F25", true);
            extrude(context, id + "F26", {"entities" : qUnion([Q0]), "operationType" : NewBodyOperationType.ADD, "depth" : 30.48 * mm});
        }
        {
            var Q0;
            Q0=makeQuery(id+"F14.opExtrude","CAP_FACE",FACE,{"disambiguationData":[OSD([sQuery(id+"F13.wireOp",EDGE,"E50.bottom"),sQuery(id+"F13.wireOp",EDGE,"E50.top"),sQuery(id+"F13.wireOp",EDGE,"E50.left"),sQuery(id+"F13.wireOp",EDGE,"E50.right")])],"isStart":false});
            var sketch = newSketch(context, id + "F27", { "sketchPlane" : qUnion([Q0])});
            skLineSegment(sketch, "E60.bottom", {"start": v(609.6, 3234.48) * mm, "end": v(1524, 3234.48) * mm});
            skLineSegment(sketch, "E60.top", {"start": v(609.6, 2929.68) * mm, "end": v(1524, 2929.68) * mm});
            skLineSegment(sketch, "E60.left", {"start": v(609.6, 3234.48) * mm, "end": v(609.6, 2929.68) * mm});
            skLineSegment(sketch, "E60.right", {"start": v(1524, 3234.48) * mm, "end": v(1524, 2929.68) * mm});
            skLineSegment(sketch, "E61.bottom", {"start": v(0, -1337.52) * mm, "end": v(1524, -1337.52) * mm});
            skLineSegment(sketch, "E61.top", {"start": v(0, -1642.32) * mm, "end": v(1524, -1642.32) * mm});
            skLineSegment(sketch, "E61.left", {"start": v(0, -1337.52) * mm, "end": v(0, -1642.32) * mm});
            skLineSegment(sketch, "E61.right", {"start": v(1524, -1337.52) * mm, "end": v(1524, -1642.32) * mm});
            skSolve(sketch);
        }
        {
            var Q0;
            Q0 = qSketchRegion(id + "F27", true);
            extrude(context, id + "F28", {"entities" : qUnion([Q0]), "depth" : 304.8 * mm});
        }
        {
            var Q0;
            Q0=makeQuery(id+"F16.opExtrude","CAP_FACE",FACE,{"disambiguationData":[OSD([sQuery(id+"F15.wireOp",EDGE,"E51.bottom"),sQuery(id+"F15.wireOp",EDGE,"E51.top"),sQuery(id+"F15.wireOp",EDGE,"E51.left"),sQuery(id+"F15.wireOp",EDGE,"E51.right")])],"isStart":false});
            var sketch = newSketch(context, id + "F29", { "sketchPlane" : qUnion([Q0])});
            skLineSegment(sketch, "E62.bottom", {"start": v(7924.8, 4758.48) * mm, "end": v(9448.8, 4758.48) * mm});
            skLineSegment(sketch, "E62.top", {"start": v(7924.8, 4728) * mm, "end": v(9448.8, 4728) * mm});
            skLineSegment(sketch, "E62.left", {"start": v(7924.8, 4758.48) * mm, "end": v(7924.8, 4728) * mm});
            skLineSegment(sketch, "E62.right", {"start": v(9448.8, 4758.48) * mm, "end": v(9448.8, 4728) * mm});
            skSolve(sketch);
        }
        {
            var Q0;
            Q0 = qSketchRegion(id + "F29", true);
            extrude(context, id + "F30", {"entities" : qUnion([Q0]), "depth" : 1828.8 * mm});
        }
        {
            var Q0;
            Q0=makeQuery(id+"F5.opExtrude","CAP_FACE",FACE,{"disambiguationData":[OSD([sQuery(id+"F4.wireOp",EDGE,"E34.bottom"),sQuery(id+"F4.wireOp",EDGE,"E34.top"),sQuery(id+"F4.wireOp",EDGE,"E34.left"),sQuery(id+"F4.wireOp",EDGE,"E34.right")])],"isStart":false});
            var sketch = newSketch(context, id + "F31", { "sketchPlane" : qUnion([Q0])});
            skLineSegment(sketch, "E63.bottom", {"start": v(3962.4, 4758.48) * mm, "end": v(6096, 4758.48) * mm});
            skLineSegment(sketch, "E63.top", {"start": v(3962.4, 4683.97) * mm, "end": v(6096, 4683.97) * mm});
            skLineSegment(sketch, "E63.left", {"start": v(3962.4, 4758.48) * mm, "end": v(3962.4, 4683.97) * mm});
            skLineSegment(sketch, "E63.right", {"start": v(6096, 4758.48) * mm, "end": v(6096, 4683.97) * mm});
            skSolve(sketch);
        }
        {
            var Q0;
            Q0 = qSketchRegion(id + "F31", true);
            extrude(context, id + "F32", {"entities" : qUnion([Q0]), "depth" : 1828.8 * mm});
        }
    });
